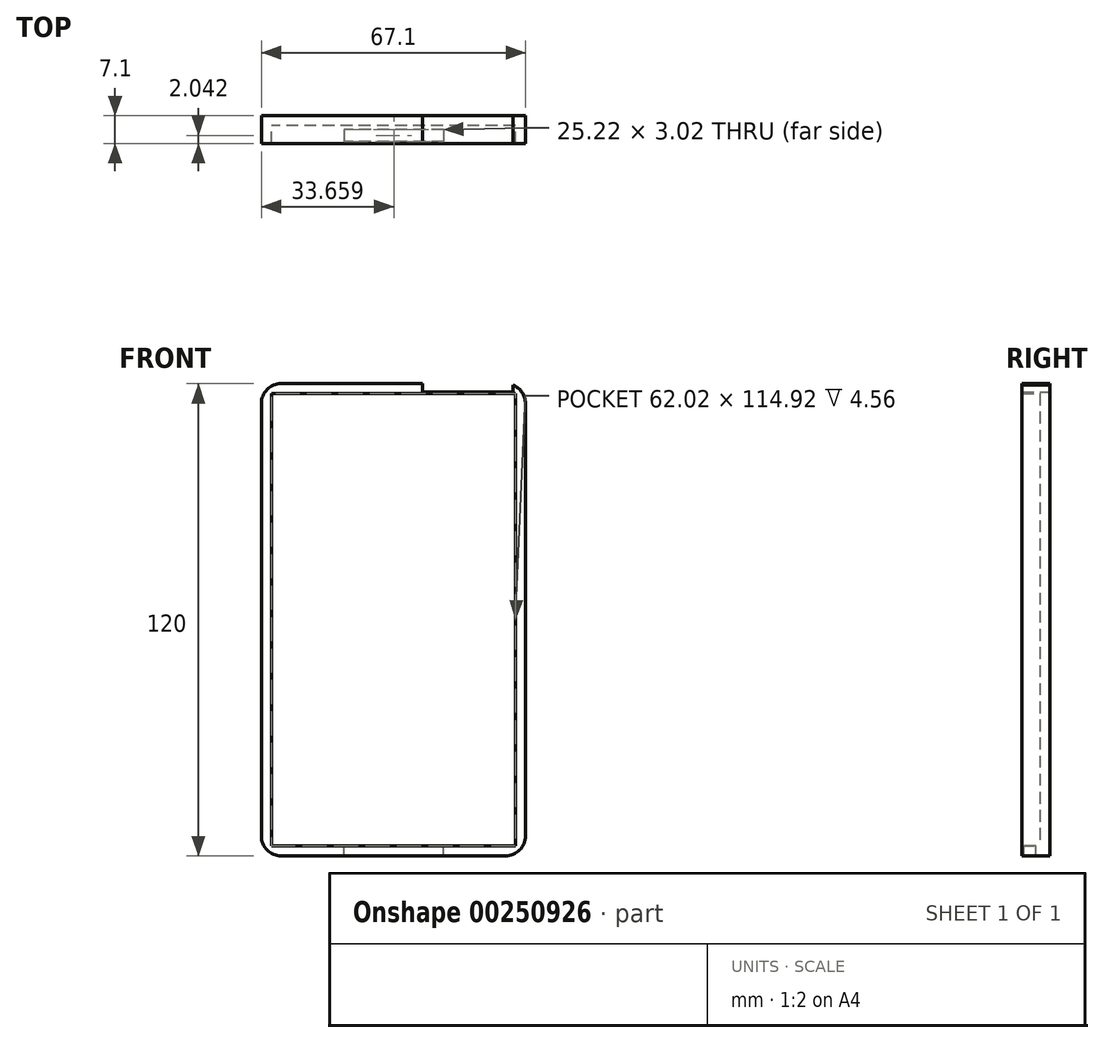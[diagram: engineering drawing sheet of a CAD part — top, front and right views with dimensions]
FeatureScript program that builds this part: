
annotation { "Feature Type Name" : "Feature", "Feature Type Description" : "" }
export const myFeature = defineFeature(function(context is Context, id is Id, definition is map)
    precondition{}
    {
        {
            var Q0;
            Q0=qCreatedBy(makeId("Front.planeOp"),FACE);
            var sketch = newSketch(context, id + "F0", { "sketchPlane" : qUnion([Q0])});
            skLineSegment(sketch, "E0.bottom", {"start": v(33.55, 60) * mm, "end": v(-33.55, 60) * mm});
            skLineSegment(sketch, "E0.top", {"start": v(33.55, -60) * mm, "end": v(-33.55, -60) * mm});
            skLineSegment(sketch, "E0.left", {"start": v(33.55, 60) * mm, "end": v(33.55, -60) * mm});
            skLineSegment(sketch, "E0.right", {"start": v(-33.55, 60) * mm, "end": v(-33.55, -60) * mm});
            skPoint(sketch, "E0.middle", {"position": v(0, 0) * mm});
            skSolve(sketch);
        }
        {
            var Q0;
            Q0=makeQuery(id+"F0.imprint","IMPRINT",FACE,{"disambiguationData":[TD([[makeQuery(id+"F0.imprint","IMPRINT",EDGE,{"derivedFrom":sQuery(id+"F0.wireOp",EDGE,"E0.bottom")}),1.0]])]});
            extrude(context, id + "F1", {"entities" : qUnion([Q0]), "endBound" : BoundingType.SYMMETRIC, "depth" : 7.1 * mm});
        }
        {
            var Q0;
            Q0=makeQuery(id+"F1.opExtrude","CAP_FACE",FACE,{"disambiguationData":[OSD([sQuery(id+"F0.wireOp",EDGE,"E0.bottom"),sQuery(id+"F0.wireOp",EDGE,"E0.top"),sQuery(id+"F0.wireOp",EDGE,"E0.left"),sQuery(id+"F0.wireOp",EDGE,"E0.right")])],"isStart":false});
            shell(context, id + "F2", {"entities" : qUnion([Q0]), "thickness" : 2.54 * mm});
        }
        {
            var Q0;
            Q0=makeQuery(id+"F1.opExtrude","SWEPT_EDGE",EDGE,{"disambiguationData":[OSD([sQuery(id+"F0.wireOp",EDGE,"E0.bottom"),sQuery(id+"F0.wireOp",EDGE,"E0.left")])]});
            fillet(context, id + "F3", {"entities" : qUnion([Q0]), "radius" : 5.08 * mm, "tangentPropagation" : true, "allowEdgeOverflow" : false});
        }
        {
            var Q0;
            Q0=makeQuery(id+"F1.opExtrude","SWEPT_EDGE",EDGE,{"disambiguationData":[OSD([sQuery(id+"F0.wireOp",EDGE,"E0.bottom"),sQuery(id+"F0.wireOp",EDGE,"E0.right")])]});
            fillet(context, id + "F4", {"entities" : qUnion([Q0]), "radius" : 5.08 * mm, "tangentPropagation" : true, "allowEdgeOverflow" : false});
        }
        {
            var Q0;
            Q0=makeQuery(id+"F1.opExtrude","SWEPT_EDGE",EDGE,{"disambiguationData":[OSD([sQuery(id+"F0.wireOp",EDGE,"E0.top"),sQuery(id+"F0.wireOp",EDGE,"E0.right")])]});
            fillet(context, id + "F5", {"entities" : qUnion([Q0]), "radius" : 5.08 * mm, "tangentPropagation" : true, "allowEdgeOverflow" : false});
        }
        {
            var Q0;
            Q0=makeQuery(id+"F1.opExtrude","SWEPT_EDGE",EDGE,{"disambiguationData":[OSD([sQuery(id+"F0.wireOp",EDGE,"E0.top"),sQuery(id+"F0.wireOp",EDGE,"E0.left")])]});
            fillet(context, id + "F6", {"entities" : qUnion([Q0]), "radius" : 5.08 * mm, "tangentPropagation" : true, "allowEdgeOverflow" : false});
        }
        {
            var Q0;
            Q0=qCreatedBy(makeId("Front.planeOp"),FACE);
            var sketch = newSketch(context, id + "F7", { "sketchPlane" : qUnion([Q0])});
            skLineSegment(sketch, "E1.bottom", {"start": v(30.4, 65.84) * mm, "end": v(7.46, 65.84) * mm});
            skLineSegment(sketch, "E1.top", {"start": v(30.4, 57.8) * mm, "end": v(7.46, 57.8) * mm});
            skLineSegment(sketch, "E1.left", {"start": v(30.4, 65.84) * mm, "end": v(30.4, 57.8) * mm});
            skLineSegment(sketch, "E1.right", {"start": v(7.46, 65.84) * mm, "end": v(7.46, 57.8) * mm});
            skSolve(sketch);
        }
        {
            var Q0;
            Q0=makeQuery(id+"F7.imprint","IMPRINT",FACE,{"disambiguationData":[TD([[makeQuery(id+"F7.imprint","IMPRINT",EDGE,{"derivedFrom":sQuery(id+"F7.wireOp",EDGE,"E1.bottom")}),1.0]])]});
            extrude(context, id + "F8", {"entities" : qUnion([Q0]), "operationType" : NewBodyOperationType.REMOVE, "endBound" : BoundingType.SYMMETRIC, "depth" : 25 * mm});
        }
        {
            var Q0;
            Q0=makeQuery(id+"F1.opExtrude","SWEPT_FACE",FACE,{"disambiguationData":[OSD([sQuery(id+"F0.wireOp",EDGE,"E0.top")])]});
            var sketch = newSketch(context, id + "F9", { "sketchPlane" : qUnion([Q0])});
            skLineSegment(sketch, "E2.bottom", {"start": v(-12.5, 3.02) * mm, "end": v(12.72, 3.02) * mm});
            skLineSegment(sketch, "E2.top", {"start": v(-12.5, 0) * mm, "end": v(12.72, 0) * mm});
            skLineSegment(sketch, "E2.left", {"start": v(-12.5, 3.02) * mm, "end": v(-12.5, 0) * mm});
            skLineSegment(sketch, "E2.right", {"start": v(12.72, 3.02) * mm, "end": v(12.72, 0) * mm});
            skSolve(sketch);
        }
        {
            var Q0;
            Q0=makeQuery(id+"F9.imprint","IMPRINT",FACE,{"disambiguationData":[TD([[makeQuery(id+"F9.imprint","IMPRINT",EDGE,{"derivedFrom":sQuery(id+"F9.wireOp",EDGE,"E2.bottom")}),-1.0]])]});
            extrude(context, id + "F10", {"entities" : qUnion([Q0]), "operationType" : NewBodyOperationType.REMOVE, "endBound" : BoundingType.SYMMETRIC, "depth" : 25 * mm});
        }
    });
